# Revit family: Módulo de 2 entradas vigiladas_Aguilera Electronica
name_source: partatom
category: Dispositivos de alarma de incendios
revit_build: Autodesk Revit 2017 (Build: 20160225_1515(x64)
units: mm (PartAtom-declared; Revit-internal decimal feet)

## family parameters
Anfitrión = Cara
Compartido = No
Corte con vacíos al cargar = No
Cota de conector redondo = Diámetro de uso
Mantener orientación de anotación = Sí
Número OmniClass = 23.85.30.21
Punto de cálculo de habitación = No
Tipo de pieza = Normal
Título OmniClass = Environmental Detection/Registration

## types (1)
- Módulo de 2 entradas vigiladas
    Descripción = Su aplicación principal es la vigilancia de sistemas de alarma (Tipo 1) como se especifica en la norma UNE EN 54-13: Evaluación de la compatibilidad de los componentes del sistema.
Unidad microprocesada direccionable fabricada por Aguilera Electrónica según norma EN 54-18 que controla el estado de 2 entradas: activación, línea en corto y línea en abierto.
    Diámetro tubo = 20 mm  [stored 0.0656168 ft]
    Elevación por defecto = 1200 mm
    Fabricante = Aguilera Electrónica
    Modelo = AE/SA-2EV
    Símbolo = Sí
    Símbolo texto modelo = Sí
    URL = http://aguilera.es

note: [stored X ft] marks values corroborated as IEEE doubles in the binary element streams (Revit-internal decimal feet)
